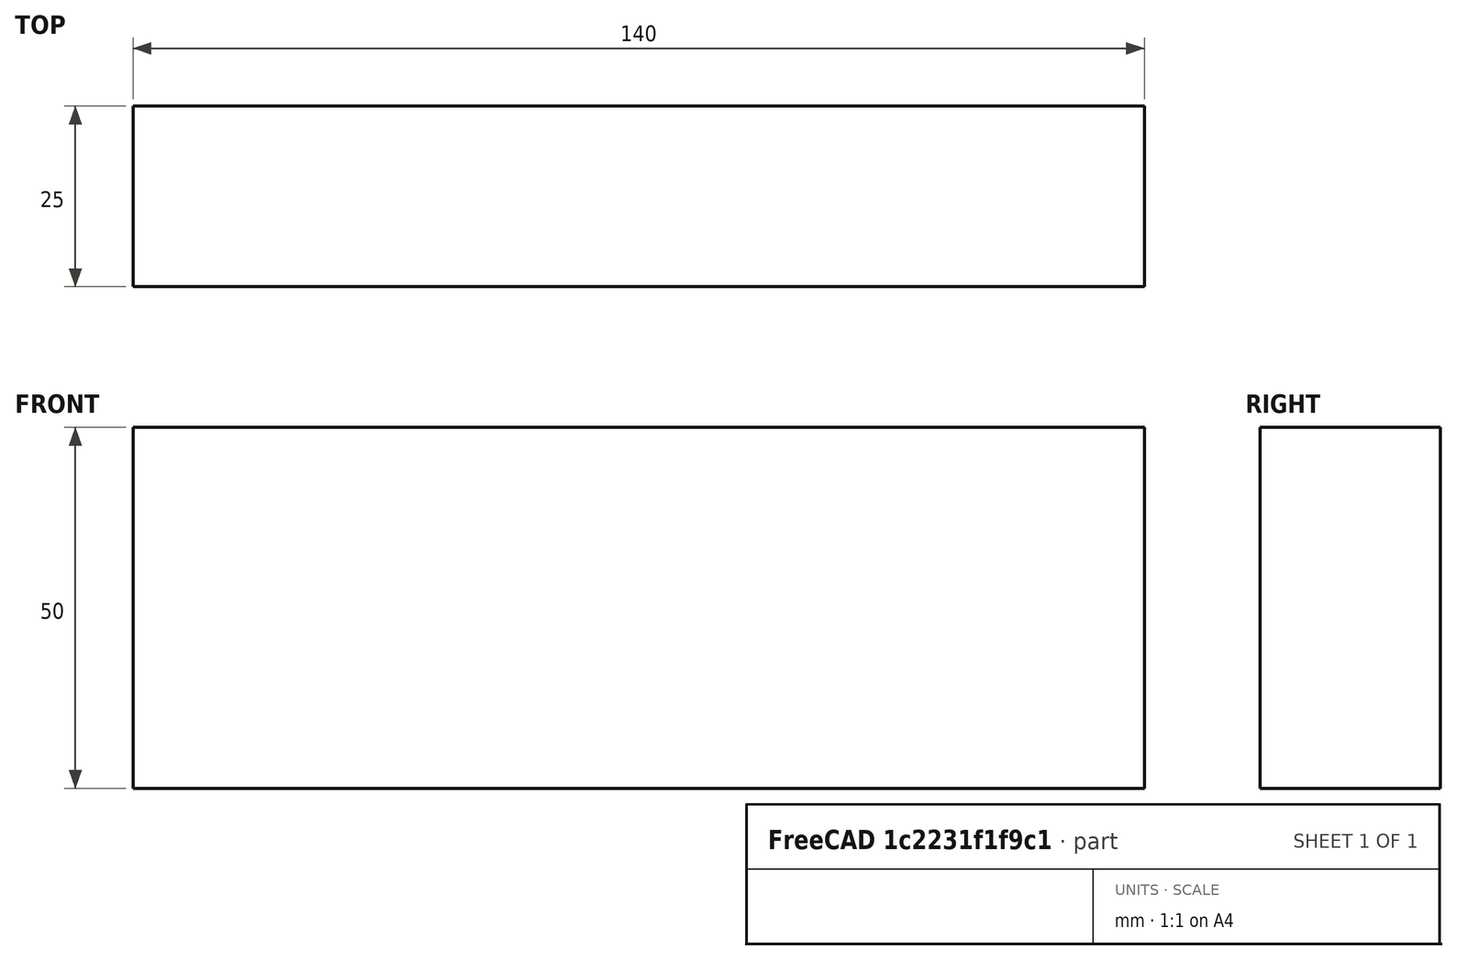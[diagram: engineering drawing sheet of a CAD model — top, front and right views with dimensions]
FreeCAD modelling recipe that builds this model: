
FCSTD DOCUMENT  (FreeCAD 0.15R4671 (Git))
Label: Flat Bar 140x25 EN10058 S235JR
License: All rights reserved
LicenseURL: http://en.wikipedia.org/wiki/All_rights_reserved
objects: Sketcher::SketchObject×1, Part::Extrusion×1
note: 2 computed .brp shape members not serialized (recipe doc carries the construction recipe); baked Part::Feature solids carry a one-line shape summary decoded from their .brp

FEATURE [Sketcher::SketchObject] Sketch
  sketch-geometry (4):
    g0: LineSegment StartX=-70 StartY=-12.5 StartZ=0 EndX=70 EndY=-12.5 EndZ=0
    g1: LineSegment StartX=70 StartY=-12.5 StartZ=0 EndX=70 EndY=12.5 EndZ=0
    g2: LineSegment StartX=70 StartY=12.5 StartZ=0 EndX=-70 EndY=12.5 EndZ=0
    g3: LineSegment StartX=-70 StartY=12.5 StartZ=0 EndX=-70 EndY=-12.5 EndZ=0
  constraints (12):
    c: Coincident(g0,g1)
    c: Coincident(g1,g2)
    c: Coincident(g2,g3)
    c: Coincident(g3,g0)
    c: Horizontal(g0)
    c: Horizontal(g2)
    c: Vertical(g1)
    c: Vertical(g3)
    c: Symmetric(g1,g2,g-2)
    c: Symmetric(g0,g1,g-1)
    c: DistanceY(g1) = 25
    c: DistanceX(g0) = 140
FEATURE [Part::Extrusion] Extrude  label="Flat Bar 140x25 EN10058 S235JR"
  Base = -> Sketch
  Dir = (0,0,50)
  Solid = true
